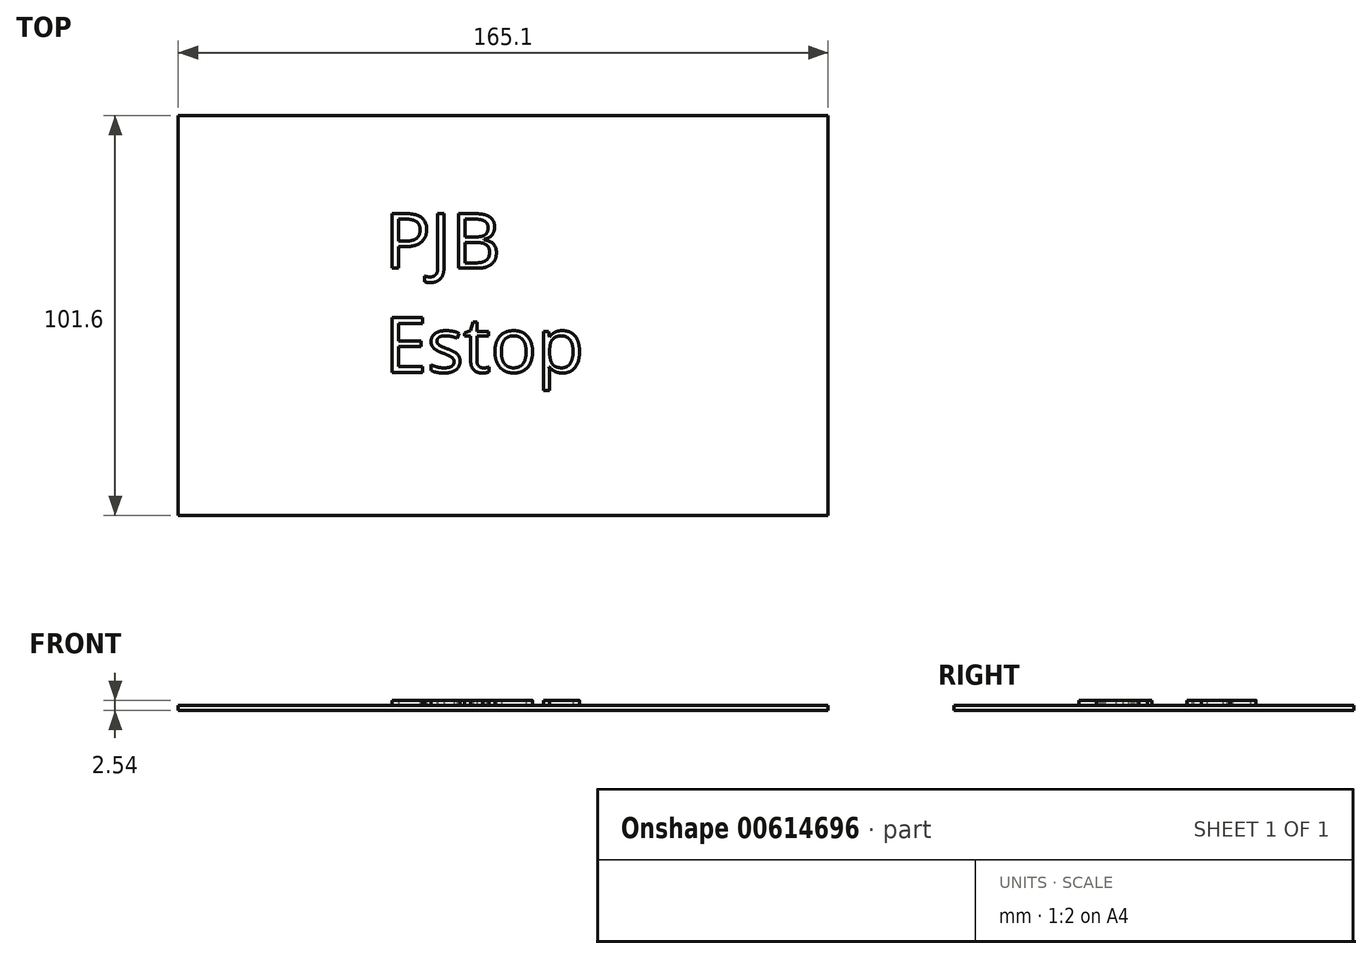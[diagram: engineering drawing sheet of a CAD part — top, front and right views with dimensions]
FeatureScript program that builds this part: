
annotation { "Feature Type Name" : "Feature", "Feature Type Description" : "" }
export const myFeature = defineFeature(function(context is Context, id is Id, definition is map)
    precondition{}
    {
        {
            var Q0;
            Q0=qCreatedBy(makeId("Top.planeOp"),FACE);
            var sketch = newSketch(context, id + "F0", { "sketchPlane" : qUnion([Q0])});
            skLineSegment(sketch, "E0.bottom", {"start": v(-71.84, 44.38) * mm, "end": v(93.26, 44.38) * mm});
            skLineSegment(sketch, "E0.top", {"start": v(-71.84, -57.22) * mm, "end": v(93.26, -57.22) * mm});
            skLineSegment(sketch, "E0.left", {"start": v(-71.84, 44.38) * mm, "end": v(-71.84, -57.22) * mm});
            skLineSegment(sketch, "E0.right", {"start": v(93.26, 44.38) * mm, "end": v(93.26, -57.22) * mm});
            skSolve(sketch);
        }
        {
            var Q0;
            Q0=makeQuery(id+"F0.imprint","IMPRINT",FACE,{"disambiguationData":[TD([[makeQuery(id+"F0.imprint","IMPRINT",EDGE,{"derivedFrom":sQuery(id+"F0.wireOp",EDGE,"E0.bottom")}),-1.0]])]});
            extrude(context, id + "F1", {"entities" : qUnion([Q0]), "depth" : 1.27 * mm, "offsetDistance" : 25.4 * mm});
        }
        {
            var Q0;
            Q0=makeQuery(id+"F1.opExtrude","CAP_FACE",FACE,{"disambiguationData":[OSD([sQuery(id+"F0.wireOp",EDGE,"E0.bottom"),sQuery(id+"F0.wireOp",EDGE,"E0.top"),sQuery(id+"F0.wireOp",EDGE,"E0.left"),sQuery(id+"F0.wireOp",EDGE,"E0.right")])],"isStart":false});
            var sketch = newSketch(context, id + "F2", { "sketchPlane" : qUnion([Q0])});
            skText(sketch, "E1", { "text": "PJB\nEstop", "fontName": "OpenSans-Regular.ttf"});
            const initialGuessF2  = {"E1": [-0.01943, 0.00558, 1, 0, 0.014]};
            skSetInitialGuess(sketch, initialGuessF2);
            skSolve(sketch);
        }
        {
            var Q0;
            Q0 = qSketchRegion(id + "F2", true);
            extrude(context, id + "F3", {"entities" : qUnion([Q0]), "operationType" : NewBodyOperationType.ADD, "depth" : 1.27 * mm, "offsetDistance" : 25.4 * mm});
        }
    });
